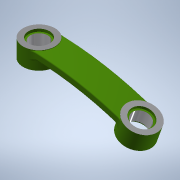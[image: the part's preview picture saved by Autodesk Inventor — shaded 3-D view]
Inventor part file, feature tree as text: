
AUTODESK INVENTOR PART (.ipt)
format: ipt  version: 2020.1 (Build 241239000, 239)  size: 304,128 bytes
history: native  units: mm
features: hole x6, sketch x5, plane x3, extrude x3, fillet x3, other x2, thicken_offset x1, revolve x1
ambient origin geometry x8: Origin, YZ Plane, XZ Plane, XY Plane, X Axis, Y Axis, Z Axis, Center Point
bodies: Solid1 (feature_tree)
feature tree (24):
  sketch  "3D Sketch1"
  plane  "Work Plane1"
  sketch  "Sketch2"  dims[d2=170.0mm d4=170.0mm]
  thicken_offset  "Thicken1"
  extrude  "Extrusion1"  TaperAngle=180.0deg  [1 undecoded]
  plane  "Work Plane2"
  extrude  "Extrusion2"  Depth=170.0mm
  plane  "Work Plane3"
  extrude  "Extrusion3"  Depth=4.0mm
  hole  "Hole1"  [1 undecoded]
  hole  "Hole2"  [1 undecoded]
  fillet  "Fillet1"  Radius=18.0mm
  fillet  "Fillet2"  Radius=10.0mm
  fillet  "Fillet3"  Radius=10.0mm
  hole  "Hole4"  [1 undecoded]
  hole  "Hole5"  [1 undecoded]
  hole  "Hole6"  [1 undecoded]
  hole  "Hole7"  [1 undecoded]
  sketch  "Sketch1"  dims[d0=170.0mm d1=180.0deg]
  other  "Srf1"
  sketch  "Sketch3"  dims[d5=16.0mm d6=4.0mm d7=8.0mm]
  sketch  "Sketch4"  dims[d8=10.0mm d9=0.0mm d10=18.0mm d11=10.0mm d12=0.0mm d13=18.0mm d14=10.0mm d15=0.0mm d16=10.0mm d17=10.0mm d18=10.0mm d19=6.0mm d20=4.0mm d21=2.0mm d22=90.0deg d23=8.0mm d24=20.594885mm d25=10.0mm d26=10.0mm d27=10.0mm d28=6.0mm d29=4.0mm d30=2.0mm d31=90.0deg d32=8.0mm d33=20.594885mm d34=1.0mm d35=10.0mm d36=0.7mm d52=3.490659mm d53=10.0mm d54=10.0mm d55=12.0mm d56=6.0mm d57=4.0mm d58=2.0mm d59=90.0deg d60=1.5mm d61=0.0mm d62=10.0mm d63=10.0mm d64=12.0mm d65=6.0mm d66=4.0mm d67=2.0mm d68=90.0deg d69=1.5mm d70=0.0mm d71=10.0mm d72=10.0mm d73=12.0mm d74=6.0mm d75=4.0mm d76=2.0mm d77=90.0deg d78=1.5mm d79=0.0mm d80=10.0mm d81=10.0mm d82=12.0mm d83=6.0mm d84=4.0mm d85=2.0mm d86=90.0deg d87=1.5mm d88=0.0mm]
  revolve  "RevolutionSrf1"  [1 undecoded]
  other  "3D Intersection1"
note: 8 required parameter values undecoded (feature->parameter linkage not recoverable at this tier; creation-order binding heuristic only, values carry confidence <= 0.55)